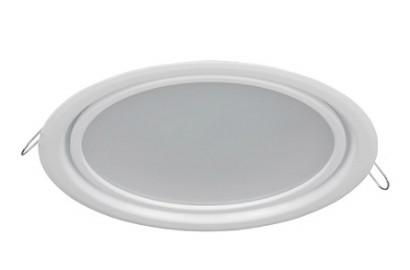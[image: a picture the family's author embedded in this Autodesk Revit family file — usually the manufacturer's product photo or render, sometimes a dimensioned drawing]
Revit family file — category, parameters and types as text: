
# Revit family: GALAD Пиксель LED
name_source: partatom
category: Осветительные приборы
revit_build: Autodesk Revit 2018 (Build: 20180423_1000(x64)
units: mm (PartAtom-declared; Revit-internal decimal feet)

## family parameters
Источник света = Да
Общий = Нет
Основа = Грань
При загрузке вырезать с полостями = Да
Размер круглого соединителя = Использовать диаметр
Тип детали = Нормальный
Точка расчета площади = Нет

## types (2) — shared parameters
ADSK_Версия Revit = 2018
ADSK_Версия семейства = 1.01
ADSK_Единица измерения = шт.
ADSK_Классификация нагрузок = Освещение
ADSK_Количество = 1
ADSK_Количество фаз = 1
ADSK_Коэффициент мощности = 0.95
ADSK_Масса = 0.6
ADSK_Масса_Текст = 0.6
ADSK_Напряжение = 230 В
ADSK_Обозначение = ГОСТ 15150-69
ADSK_Размер_Высота = 30 мм
ADSK_Размер_Длина = 250 мм
ADSK_Размер_Ширина = 250 мм
ADSK_Ток = 0 А
IP = 20
URL = https://galad.ru
Видимая форма излучения при визуализации = Нет
Возможный угол наклона = 0
Группа модели = Светильники
Диапазон цветовой температуры = 3985±275
Изготовитель = АО «КАДОШКИНСКИЙ ЭЛЕКТРОТЕХНИЧЕСКИЙ ЗАВОД»
Излучение по диаметру окружности = 210 мм
Класс Защиты = 1
Класс защиты от поражения электрическим током = 1
Класс светораспределения = П
Климатическая зона = УХЛ4
Климатическое исполнение = 1…35 °С
Коэффициент пульсации = менее 5%
Материал корпуса = Сталь
Материал рассеивателя = ПММА
Описание = GALAD Пиксель LED - это бюджетная серия светильников типа downlight, широко востребованных как в офисном, так и в торговом освещении. Пиксель не рассеивает свет по сторонам, а направляет световой пучок исключительно вниз, что дает возможность акцентировать внимание и высветлить отдельные зоны пространства.
Отметка по умолчанию = 1219 мм
Световая отдача = 74
Светофильтр = 16777215
Смещение цветовой температуры при затухании лампы = <Нет>
Снижение светового потока во время разгорания = не более 6%
Срок службы = 12 лет
Тип КСС = Косинусная
Тип ПРА = ЭПРА
Тип источника света = LED
Тип монтажной поверхности = потолок
Тип продукции = Светильник
Тип устройства управления светодиодами = без управления
Угол наклона = 90.00°
Цветопередача = 80
Частота = 50
zero-valued in all types: Неравномерность яркости

## per-type parameters (varying)
| type | ADSK_Код изделия | ADSK_Номинальная мощность | ADSK_Полная мощность | ADSK_Энергоэффективность | Полная установленная мощность | Файл фотометрической сетки |
| GALAD Пиксель LED-24-d250/В/М/4000 | 11917 | 24 В·А | 25 В·А | 74 лм/Вт | 25 В·А | GALAD piksel LED-24-d250_v_m_5000.IES |
| GALAD Пиксель LED-18-d250/В/М/4000 | 10733 | 18 В·А | 19 В·А | 79 лм/Вт | 19 В·А | GALAD piksel LED-18-d250_v_m_4000.IES |

note: column(s) folded — value = type name in every type: ADSK_Марка, ADSK_Наименование, ADSK_Наименование краткое
